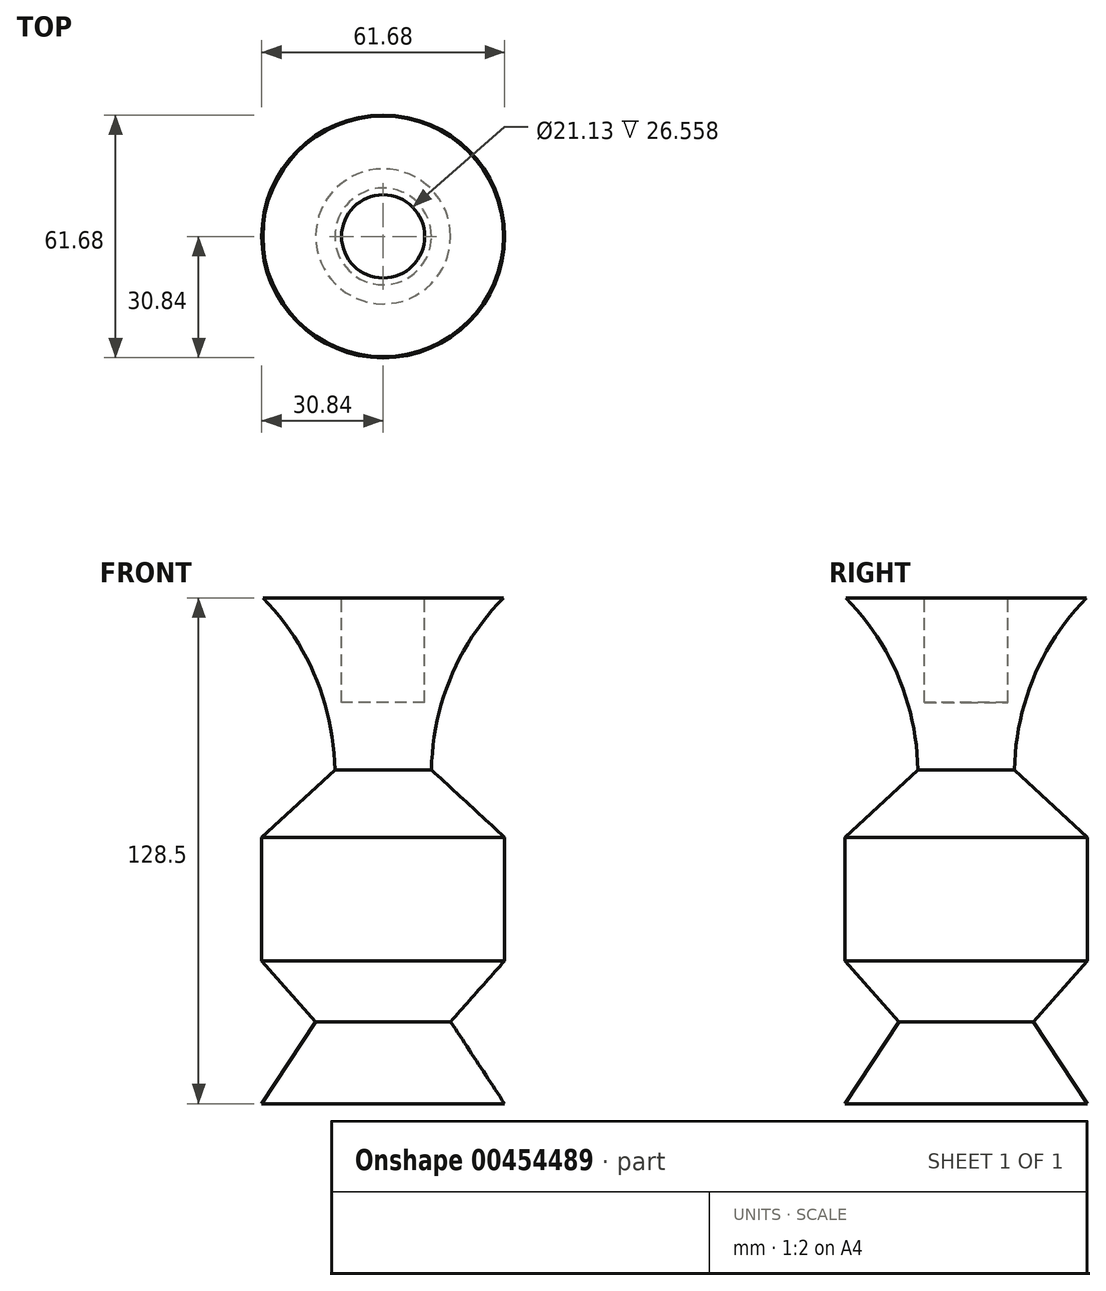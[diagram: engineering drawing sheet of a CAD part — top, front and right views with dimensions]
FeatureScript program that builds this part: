
annotation { "Feature Type Name" : "Feature", "Feature Type Description" : "" }
export const myFeature = defineFeature(function(context is Context, id is Id, definition is map)
    precondition{}
    {
        {
            var Q0;
            Q0=qCreatedBy(makeId("Front.planeOp"),FACE);
            var sketch = newSketch(context, id + "F0", { "sketchPlane" : qUnion([Q0])});
            skLineSegment(sketch, "E0", {"start": v(0, 75.68) * mm, "end": v(0, -62.25) * mm});
            skLineSegment(sketch, "E1", {"start": v(0, -62.25) * mm, "end": v(30.84, -62.25) * mm});
            skLineSegment(sketch, "E2", {"start": v(17.13, -41.4) * mm, "end": v(30.84, -62.25) * mm});
            skLineSegment(sketch, "E3", {"start": v(17.13, -41.4) * mm, "end": v(30.84, -25.99) * mm});
            skLineSegment(sketch, "E4", {"start": v(30.84, -25.99) * mm, "end": v(30.84, 5.43) * mm});
            skLineSegment(sketch, "E5", {"start": v(30.84, 5.43) * mm, "end": v(12.28, 22.56) * mm});
            skArc(sketch, "E6", {"start": v(30.56, 66.25) * mm, "mid": v(17.2, 46.17) * mm, "end": v(12.28, 22.56) * mm});
            skLineSegment(sketch, "E7", {"start": v(30.56, 66.25) * mm, "end": v(10.57, 66.25) * mm});
            skLineSegment(sketch, "E8", {"start": v(10.57, 66.25) * mm, "end": v(10.57, 39.7) * mm});
            skLineSegment(sketch, "E9", {"start": v(10.57, 39.7) * mm, "end": v(0, 39.7) * mm});
            skSolve(sketch);
        }
        {
            var Q0;
            {var subQ0=sQuery(id+"F0.wireOp",EDGE,"E1");Q0=makeQuery(id+"F0.imprint","IMPRINT",FACE,{"disambiguationData":[TD([[makeQuery(id+"F0.imprint","IMPRINT",EDGE,{"derivedFrom":subQ0}),1.0]])]});}
            var Q1;
            Q1=sQuery(id+"F0.wireOp",EDGE,"E0");
            revolve(context, id + "F1", {"entities" : qUnion([Q0]), "axis" : qUnion([Q1]), "revolveType" : RevolveType.FULL});
        }
    });
